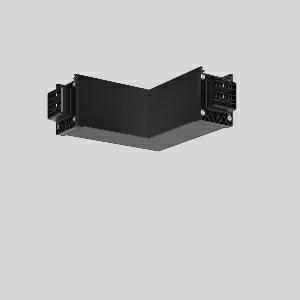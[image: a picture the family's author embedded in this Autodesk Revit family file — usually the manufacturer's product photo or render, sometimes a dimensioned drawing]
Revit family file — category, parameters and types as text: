
# Revit family: linedo_l-verbindung_982773_003_2_2c30
name_source: partatom
category: Lighting Fixtures
units: mm (PartAtom-declared; Revit-internal decimal feet)

## family parameters
Cut with Voids When Loaded = No
Host = Face
Light Source = No
Part Type = Normal
Room Calculation Point = No
Round Connector Dimension = Use Diameter
Shared = No

## types (1)
- LINEDO L-Verbindung
    Apparent Load = 0 VA
    Default Elevation = 1800 mm
    Description = Series: LINEDO
L-connector, 14-pole, connection plug / plug. Housing: extruded aluminium profile, powder-coated. Cover made of plastic, surface like housing. LINEDO plug system, plastic, black. Easy connection for rigid or flexible wires. 2 membrane cable entries (M25). Suitable for power supply in 7-pole version. Ready prewired. Colour-coded individual cables enable easy electromechanical separation.
Colour: jet black (RAL 9005)
Length: 204 mm
Width: 204 mm
Height: 76 mm
Weight: 730 g
    Height = 76 mm
    Lamp = 0 x
    Length = 204 mm
    Luminous efficacy = 0 lm/W
    Manufacturer = RZB
    ModVariant = No
    Model = 982773.003.2
    Mounting Place = Ceiling
    Mounting Type = Surface mounted
    Number of Poles = 1
    OnlyDefault = Yes
    Power Factor = 1
    Product Name = LINEDO L-Verbindung
    Product group = Surface mounted continuous line luminaire system
    ProductGroupID = 310
    Protection Class = Protection class I
    Protection Degree = Degree of protection
    RLX_Detail_Level = 1
    RLX_Emergency_Light_Flux = 0 lm
    RLX_Emergency_Type = 0
    RLX_Emergency_Type_DB = No
    RlxData = <blob elided: 19633 chars, md5=578a0aae>
    Standby Power = 0 W
    System Light Flux = 0 lm
    System Power = 0 W
    Type Comments = Product without accessories
    Type Image = 982773.003.2.jpg
    URL = http://relux.com
    VarID = ---
    Voltage = 0 V
    Weight = 0.00 kg
    Width = 204 mm

## geometry (parser evidence)
native form markers: Blend x4, Sweep x12
no freeform markers — native parametric forms only
